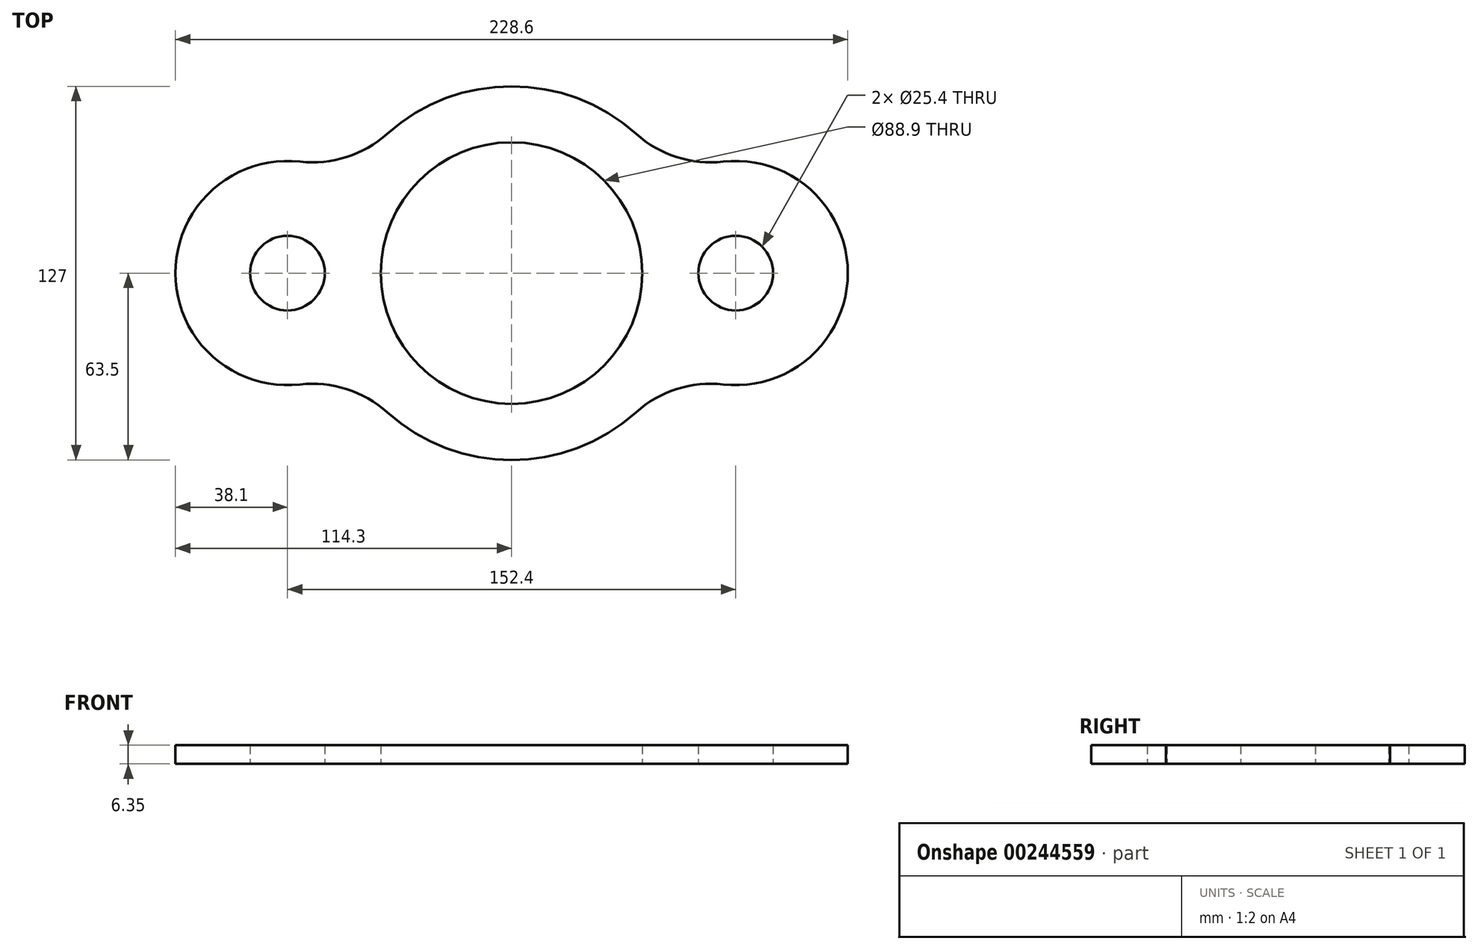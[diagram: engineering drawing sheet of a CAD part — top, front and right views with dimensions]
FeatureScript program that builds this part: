
annotation { "Feature Type Name" : "Feature", "Feature Type Description" : "" }
export const myFeature = defineFeature(function(context is Context, id is Id, definition is map)
    precondition{}
    {
        {
            var Q0;
            Q0=qCreatedBy(makeId("Top.planeOp"),FACE);
            var sketch = newSketch(context, id + "F0", { "sketchPlane" : qUnion([Q0])});
            skCircle(sketch, "E0", {"center": v(0, 0) * mm, "radius": 44.45 * mm});
            skArc(sketch, "E1", {"start": v(-42.33, -47.33) * mm, "mid": v(0, -63.5) * mm, "end": v(42.33, -47.33) * mm});
            skCircle(sketch, "E2", {"center": v(-76.2, 0) * mm, "radius": 12.7 * mm});
            skCircle(sketch, "E3", {"center": v(76.2, 0) * mm, "radius": 12.7 * mm});
            skArc(sketch, "E4", {"start": v(71.97, -37.86) * mm, "mid": v(114.3, 0) * mm, "end": v(71.97, 37.86) * mm});
            skArc(sketch, "E5", {"start": v(-71.97, 37.86) * mm, "mid": v(-114.3, 0) * mm, "end": v(-71.97, -37.86) * mm});
            skArc(sketch, "E6.trimOffspring", {"start": v(42.33, 47.33) * mm, "mid": v(0, 63.5) * mm, "end": v(-42.33, 47.33) * mm});
            skPoint(sketch, "E7.visualSharp", {"position": v(55.03, 31.68) * mm});
            skArc(sketch, "E7.filletArc", {"start": v(42.33, 47.33) * mm, "mid": v(56.14, 39.43) * mm, "end": v(71.97, 37.86) * mm});
            skPoint(sketch, "E8.visualSharp", {"position": v(55.03, -31.68) * mm});
            skArc(sketch, "E8.filletArc", {"start": v(71.97, -37.86) * mm, "mid": v(56.14, -39.43) * mm, "end": v(42.33, -47.33) * mm});
            skPoint(sketch, "E9.visualSharp", {"position": v(-55.03, -31.68) * mm});
            skArc(sketch, "E9.filletArc", {"start": v(-42.33, -47.33) * mm, "mid": v(-56.14, -39.43) * mm, "end": v(-71.97, -37.86) * mm});
            skPoint(sketch, "E10.visualSharp", {"position": v(-55.03, 31.68) * mm});
            skArc(sketch, "E10.filletArc", {"start": v(-71.97, 37.86) * mm, "mid": v(-56.14, 39.43) * mm, "end": v(-42.33, 47.33) * mm});
            skSolve(sketch);
        }
        {
            var Q0;
            Q0=makeQuery(id+"F0.imprint","IMPRINT",FACE,{"disambiguationData":[TD([[makeQuery(id+"F0.imprint","IMPRINT",EDGE,{"derivedFrom":sQuery(id+"F0.wireOp",EDGE,"E0")}),-1.0]])]});
            extrude(context, id + "F1", {"entities" : qUnion([Q0]), "depth" : 6.35 * mm});
        }
    });
